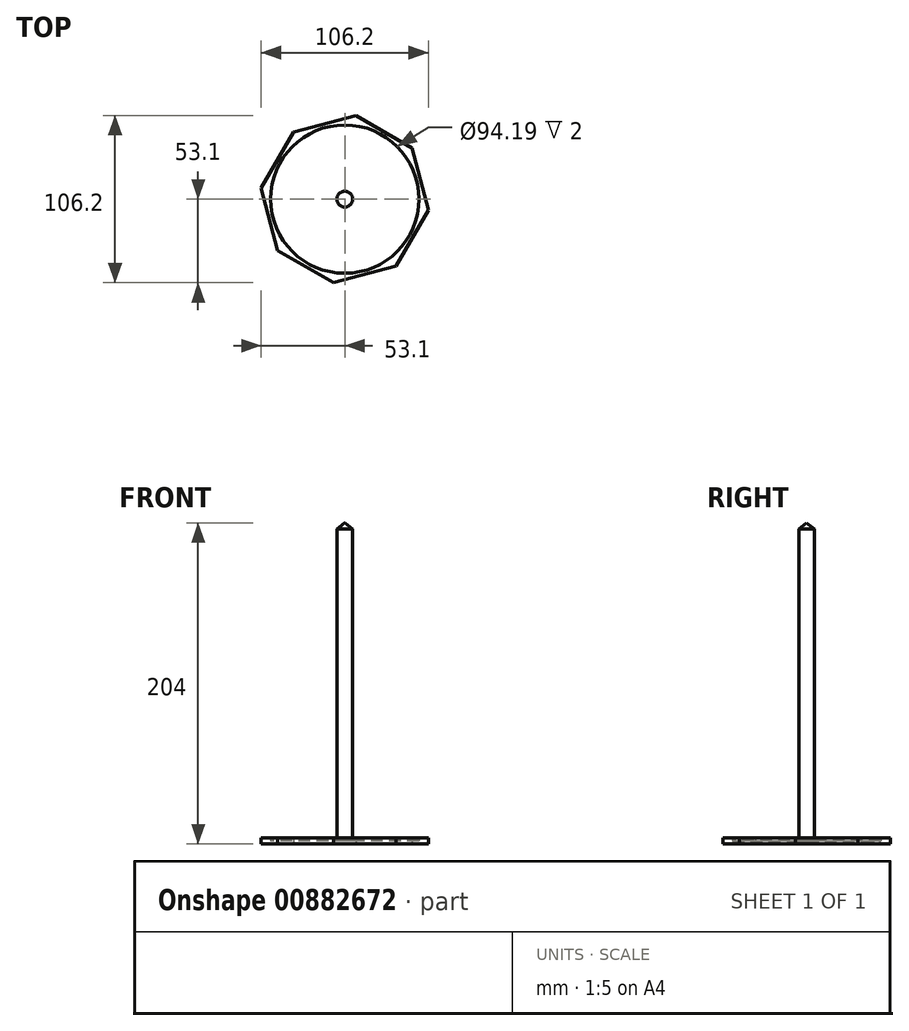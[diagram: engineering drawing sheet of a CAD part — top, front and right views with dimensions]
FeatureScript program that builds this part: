
annotation { "Feature Type Name" : "Feature", "Feature Type Description" : "" }
export const myFeature = defineFeature(function(context is Context, id is Id, definition is map)
    precondition{}
    {
        {
            var Q0;
            Q0=qCreatedBy(makeId("Top.planeOp"),FACE);
            var sketch = newSketch(context, id + "F0", { "sketchPlane" : qUnion([Q0])});
            skCircle(sketch, "E0.cCircle", {"center": v(0, 0) * mm, "radius": 49.5 * mm, "construction": true});
            skLineSegment(sketch, "E0.0", {"start": v(-53.1, 7.08) * mm, "end": v(-32.54, 42.55) * mm});
            skLineSegment(sketch, "E0.1", {"start": v(-32.54, 42.55) * mm, "end": v(7.08, 53.1) * mm});
            skLineSegment(sketch, "E0.2", {"start": v(7.08, 53.1) * mm, "end": v(42.55, 32.54) * mm});
            skLineSegment(sketch, "E0.3", {"start": v(42.55, 32.54) * mm, "end": v(53.1, -7.08) * mm});
            skLineSegment(sketch, "E0.4", {"start": v(53.1, -7.08) * mm, "end": v(32.54, -42.55) * mm});
            skLineSegment(sketch, "E0.5", {"start": v(32.54, -42.55) * mm, "end": v(-7.08, -53.1) * mm});
            skLineSegment(sketch, "E0.6", {"start": v(-7.08, -53.1) * mm, "end": v(-42.55, -32.54) * mm});
            skLineSegment(sketch, "E0.7", {"start": v(-42.55, -32.54) * mm, "end": v(-53.1, 7.08) * mm});
            skPoint(sketch, "E0.0.midPoint", {"position": v(-42.82, 24.82) * mm});
            skCircle(sketch, "E1", {"center": v(0, 0) * mm, "radius": 47.1 * mm});
            skCircle(sketch, "E2", {"center": v(0, 0) * mm, "radius": 5 * mm});
            skLineSegment(sketch, "E3", {"start": v(-32.54, 42.55) * mm, "end": v(32.54, -42.55) * mm, "construction": true});
            skLineSegment(sketch, "E4", {"start": v(42.55, 32.54) * mm, "end": v(-42.55, -32.54) * mm, "construction": true});
            skSolve(sketch);
        }
        {
            var Q0;
            Q0=makeQuery(id+"F0.imprint","IMPRINT",FACE,{"disambiguationData":[TD([[makeQuery(id+"F0.imprint","IMPRINT",EDGE,{"derivedFrom":sQuery(id+"F0.wireOp",EDGE,"E2")}),1.0]])]});
            extrude(context, id + "F1", {"entities" : qUnion([Q0]), "depth" : 200 * mm, "offsetDistance" : 25 * mm});
        }
        {
            var Q0;
            Q0=makeQuery(id+"F0.imprint","IMPRINT",FACE,{"disambiguationData":[TD([[makeQuery(id+"F0.imprint","IMPRINT",EDGE,{"derivedFrom":sQuery(id+"F0.wireOp",EDGE,"E1")}),1.0]])]});
            extrude(context, id + "F2", {"entities" : qUnion([Q0]), "operationType" : NewBodyOperationType.ADD, "depth" : 2 * mm, "offsetDistance" : 25 * mm});
        }
        {
            var Q0;
            Q0=makeQuery(id+"F0.imprint","IMPRINT",FACE,{"disambiguationData":[TD([[makeQuery(id+"F0.imprint","IMPRINT",EDGE,{"derivedFrom":sQuery(id+"F0.wireOp",EDGE,"E0.0")}),-1.0]])]});
            extrude(context, id + "F3", {"entities" : qUnion([Q0]), "operationType" : NewBodyOperationType.ADD, "depth" : 4 * mm, "offsetDistance" : 25 * mm});
        }
        {
            var Q0;
            Q0=makeQuery(id+"F1.opExtrude","CAP_FACE",FACE,{"disambiguationData":[OSD([sQuery(id+"F0.wireOp",EDGE,"E2")])],"isStart":false});
            cPlane(context, id + "F4", {"entities" : qUnion([Q0]), "cplaneType" : CPlaneType.OFFSET, "offset" : 4 * mm, "width" : 150 * mm, "height" : 150 * mm});
        }
        {
            var Q0;
            Q0=qCreatedBy(id+"F4.planeOp",FACE);
            var sketch = newSketch(context, id + "F5", { "sketchPlane" : qUnion([Q0])});
            skPoint(sketch, "E5", {"position": v(0, 0) * mm});
            skSolve(sketch);
        }
        {
            var Q1;
            Q1=sQuery(id+"F5.wireOp",VERTEX,"E5");
            var Q2;
            Q2=makeQuery(id+"F1.opExtrude","CAP_FACE",FACE,{"disambiguationData":[OSD([sQuery(id+"F0.wireOp",EDGE,"E2")])],"isStart":false});
            loft(context, id + "F6", {"operationType" : NewBodyOperationType.ADD, "sheetProfilesArray" : [{ "sheetProfileEntities" : qUnion([Q1]) }, { "sheetProfileEntities" : qUnion([Q2]) }]});
        }
    });
